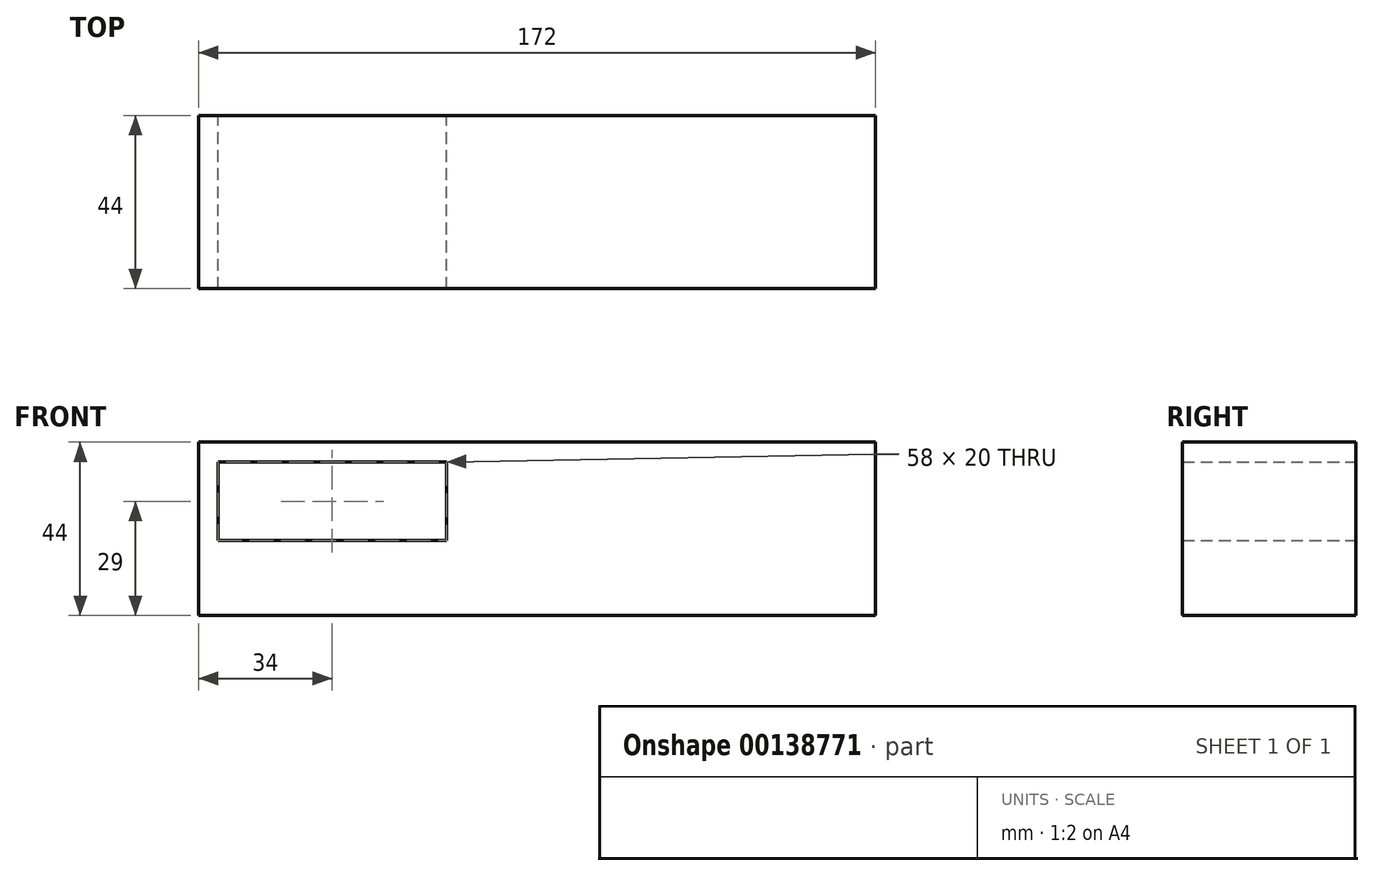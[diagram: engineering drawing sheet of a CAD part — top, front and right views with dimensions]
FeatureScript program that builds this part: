
annotation { "Feature Type Name" : "Feature", "Feature Type Description" : "" }
export const myFeature = defineFeature(function(context is Context, id is Id, definition is map)
    precondition{}
    {
        {
            var Q0;
            Q0=qCreatedBy(makeId("Front.planeOp"),FACE);
            var sketch = newSketch(context, id + "F0", { "sketchPlane" : qUnion([Q0])});
            skLineSegment(sketch, "E0.bottom", {"start": v(86, 22) * mm, "end": v(-86, 22) * mm});
            skLineSegment(sketch, "E0.top", {"start": v(86, -22) * mm, "end": v(-86, -22) * mm});
            skLineSegment(sketch, "E0.left", {"start": v(86, 22) * mm, "end": v(86, -22) * mm});
            skLineSegment(sketch, "E0.right", {"start": v(-86, 22) * mm, "end": v(-86, -22) * mm});
            skPoint(sketch, "E0.middle", {"position": v(0, 0) * mm});
            skLineSegment(sketch, "E1.bottom", {"start": v(-81, 17) * mm, "end": v(-23, 17) * mm});
            skLineSegment(sketch, "E1.top", {"start": v(-81, -3) * mm, "end": v(-23, -3) * mm});
            skLineSegment(sketch, "E1.left", {"start": v(-81, 17) * mm, "end": v(-81, -3) * mm});
            skLineSegment(sketch, "E1.right", {"start": v(-23, 17) * mm, "end": v(-23, -3) * mm});
            skSolve(sketch);
        }
        {
            var Q0;
            Q0=makeQuery(id+"F0.imprint","IMPRINT",FACE,{"disambiguationData":[TD([[makeQuery(id+"F0.imprint","IMPRINT",EDGE,{"derivedFrom":sQuery(id+"F0.wireOp",EDGE,"E0.bottom")}),1.0]])]});
            extrude(context, id + "F1", {"entities" : qUnion([Q0]), "endBound" : BoundingType.SYMMETRIC, "depth" : 44 * mm});
        }
    });
